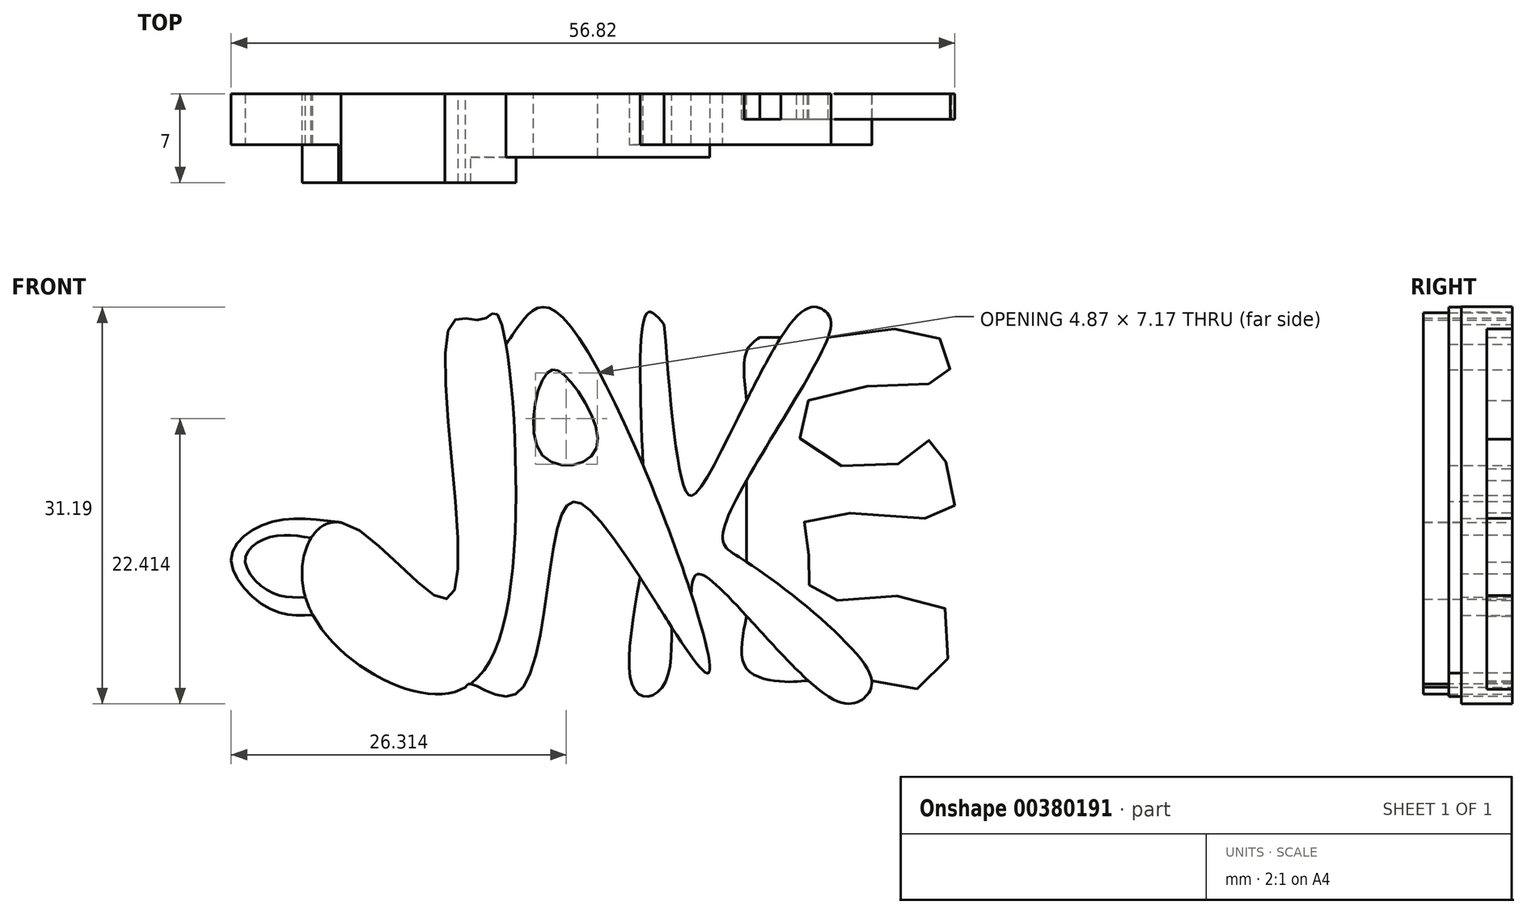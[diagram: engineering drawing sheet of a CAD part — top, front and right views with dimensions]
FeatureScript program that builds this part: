
annotation { "Feature Type Name" : "Feature", "Feature Type Description" : "" }
export const myFeature = defineFeature(function(context is Context, id is Id, definition is map)
    precondition{}
    {
        {
            var Q0;
            Q0=qCreatedBy(makeId("Front.planeOp"),FACE);
            var sketch = newSketch(context, id + "F0", { "sketchPlane" : qUnion([Q0])});
            skFitSpline(sketch, "E0", {"points": [v(-53.11, 12.85) * mm, v(-53.19, -8.62) * mm, v(-61.73, -2.73) * mm, v(-64.52, -8.6) * mm, v(-53.55, -16.19) * mm, v(-48.19, -5.6) * mm, v(-49.58, 13.73) * mm, v(-50.61, 13.22) * mm, v(-53.11, 12.85) * mm]});
            skFitSpline(sketch, "E1", {"points": [v(-48.76, 11.29) * mm, v(-47.67, 12.85) * mm, v(-44.88, 13.88) * mm, v(-32.82, -14.5) * mm, v(-41.64, -2.3) * mm, v(-44.29, -1.85) * mm, v(-47.97, -16.19) * mm, v(-51.55, -15.4) * mm, v(-51.94, -15.66) * mm], "startDerivative": vector(13.71, 20.42) * mm, "endDerivative": vector(-7.72, -12.5) * mm});
            skFitSpline(sketch, "E2", {"points": [v(-45.54, 9.03) * mm, v(-45.9, 2.56) * mm, v(-41.79, 2.85) * mm, v(-43.85, 8.51) * mm, v(-45.54, 9.03) * mm]});
            skFitSpline(sketch, "E3", {"points": [v(-36.35, 12.85) * mm, v(-37.6, 13.8) * mm, v(-38.02, 1.78) * mm], "startDerivative": vector(-5.25, 6.25) * mm, "endDerivative": vector(0.93, -23.72) * mm});
            skFitSpline(sketch, "E4", {"points": [v(-36.35, 12.85) * mm, v(-34.8, 0.13) * mm, v(-34, -0.53) * mm, v(-25.76, 13.66) * mm, v(-23.7, 13.88) * mm, v(-23.48, 11.82) * mm, v(-31.72, -3.4) * mm, v(-29.88, -5.82) * mm, v(-20.32, -14.35) * mm, v(-20.47, -16.34) * mm, v(-23.19, -16.56) * mm, v(-33.56, -6.78) * mm, v(-34.23, -8.3) * mm], "startDerivative": vector(10.34, -129.68) * mm, "endDerivative": vector(-4.62, -54.45) * mm});
            skFitSpline(sketch, "E5", {"points": [v(-35.75, -10.96) * mm, v(-36.35, -15.45) * mm, v(-37.82, -16.4) * mm, v(-38.92, -15.3) * mm, v(-38.24, -7.05) * mm], "startDerivative": vector(-0.1, -18.57) * mm, "endDerivative": vector(4.6, 26.27) * mm});
            skFitSpline(sketch, "E6", {"points": [v(-28.85, 11.82) * mm, v(-27.18, 11.82) * mm], "startDerivative": vector(1.67, 0) * mm, "endDerivative": vector(1.67, 0) * mm});
            skFitSpline(sketch, "E7", {"points": [v(-28.85, 11.82) * mm, v(-29.88, 10.72) * mm, v(-29.88, 6.86) * mm], "startDerivative": vector(-3.2, -2.21) * mm, "endDerivative": vector(0.83, -7.33) * mm});
            skFitSpline(sketch, "E8", {"points": [v(-29.88, 0.6) * mm, v(-29.88, -5.82) * mm], "startDerivative": vector(0, -6.42) * mm, "endDerivative": vector(0, -6.42) * mm});
            skFitSpline(sketch, "E9", {"points": [v(-29.88, -10.08) * mm, v(-29.88, -14.2) * mm, v(-26.94, -15.23) * mm, v(-25.03, -15.15) * mm], "startDerivative": vector(-2.59, -12.4) * mm, "endDerivative": vector(6.33, 0.7) * mm});
            skFitSpline(sketch, "E10", {"points": [v(-20.05, -15.15) * mm, v(-15.1, -15.15) * mm, v(-14.52, -9.2) * mm, v(-22.75, -8.84) * mm, v(-25.03, -7.44) * mm, v(-25.03, -4.87) * mm, v(-25.03, -2.3) * mm, v(-14.3, -2.3) * mm, v(-13.63, -0.53) * mm, v(-15.17, 3.8) * mm, v(-17.45, 2.12) * mm, v(-25.03, 3) * mm, v(-25.03, 6.86) * mm, v(-15.32, 8.22) * mm, v(-13.92, 9.25) * mm, v(-14.8, 11.82) * mm, v(-23.48, 11.82) * mm], "startDerivative": vector(85.9, -26.97) * mm, "endDerivative": vector(-126.58, -20.41) * mm});
            skFitSpline(sketch, "E11", {"points": [v(-61.73, -2.73) * mm, v(-67.31, -2.73) * mm, v(-70.35, -5.58) * mm, v(-67.36, -9.5) * mm, v(-63.95, -9.98) * mm], "startDerivative": vector(-20.48, 2.9) * mm, "endDerivative": vector(15.12, 0.94) * mm});
            skFitSpline(sketch, "E12", {"points": [v(-64.07, -3.94) * mm, v(-67.27, -3.87) * mm, v(-69.25, -5.58) * mm, v(-67.4, -8.11) * mm, v(-64.52, -8.6) * mm], "startDerivative": vector(-12.35, 2) * mm, "endDerivative": vector(11.7, 0.13) * mm});
            skSolve(sketch);
        }
        {
            var Q0;
            {var subQ0=sQuery(id+"F0.wireOp",EDGE,"E1");var subQ1=sQuery(id+"F0.wireOp",EDGE,"E0");var subQ2=makeQuery(id+"F0.imprint","INTERSECT",VERTEX,{"disambiguationData":[OD(0.0)],"derivedFrom":[subQ1,subQ0]});Q0=makeQuery(id+"F0.imprint","IMPRINT",FACE,{"disambiguationData":[TD([[makeQuery(id+"F0.imprint","IMPRINT",EDGE,{"disambiguationData":[TD([[subQ2,1.0]])],"derivedFrom":subQ1}),1.0]])]});}
            extrude(context, id + "F1", {"entities" : qUnion([Q0]), "depth" : 7 * mm});
        }
        {
            var Q0;
            Q0=makeQuery(id+"F0.imprint","IMPRINT",FACE,{"disambiguationData":[TD([[makeQuery(id+"F0.imprint","IMPRINT",EDGE,{"derivedFrom":sQuery(id+"F0.wireOp",EDGE,"E2")}),-1.0]])]});
            extrude(context, id + "F2", {"entities" : qUnion([Q0]), "operationType" : NewBodyOperationType.ADD, "depth" : 5 * mm});
        }
        {
            var Q0;
            {var subQ11=sQuery(id+"F0.wireOp",EDGE,"E3");Q0=makeQuery(id+"F0.imprint","IMPRINT",FACE,{"disambiguationData":[TD([[makeQuery(id+"F0.imprint","IMPRINT",EDGE,{"derivedFrom":subQ11}),1.0]])]});}
            var Q1;
            {var subQ0=sQuery(id+"F0.wireOp",EDGE,"E5");Q1=makeQuery(id+"F0.imprint","IMPRINT",FACE,{"disambiguationData":[TD([[makeQuery(id+"F0.imprint","IMPRINT",EDGE,{"derivedFrom":subQ0}),-1.0]])]});}
            extrude(context, id + "F3", {"entities" : qUnion([Q0, Q1]), "operationType" : NewBodyOperationType.ADD, "depth" : 4 * mm});
        }
        {
            var Q0;
            {var subQ0=sQuery(id+"F0.wireOp",EDGE,"E6");Q0=makeQuery(id+"F0.imprint","IMPRINT",FACE,{"disambiguationData":[TD([[makeQuery(id+"F0.imprint","IMPRINT",EDGE,{"derivedFrom":subQ0}),-1.0]])]});}
            var Q1;
            {var subQ0=sQuery(id+"F0.wireOp",EDGE,"E8");Q1=makeQuery(id+"F0.imprint","IMPRINT",FACE,{"disambiguationData":[TD([[makeQuery(id+"F0.imprint","IMPRINT",EDGE,{"derivedFrom":subQ0}),1.0]])]});}
            var Q2;
            {var subQ0=sQuery(id+"F0.wireOp",EDGE,"E9");Q2=makeQuery(id+"F0.imprint","IMPRINT",FACE,{"disambiguationData":[TD([[makeQuery(id+"F0.imprint","IMPRINT",EDGE,{"derivedFrom":subQ0}),1.0]])]});}
            extrude(context, id + "F4", {"entities" : qUnion([Q0, Q1, Q2]), "operationType" : NewBodyOperationType.ADD, "depth" : 2 * mm});
        }
        {
            var Q0;
            {var subQ0=sQuery(id+"F0.wireOp",EDGE,"E12");Q0=makeQuery(id+"F0.imprint","IMPRINT",FACE,{"disambiguationData":[TD([[makeQuery(id+"F0.imprint","IMPRINT",EDGE,{"derivedFrom":subQ0}),-1.0]])]});}
            extrude(context, id + "F5", {"entities" : qUnion([Q0]), "operationType" : NewBodyOperationType.ADD, "depth" : 4 * mm});
        }
    });
